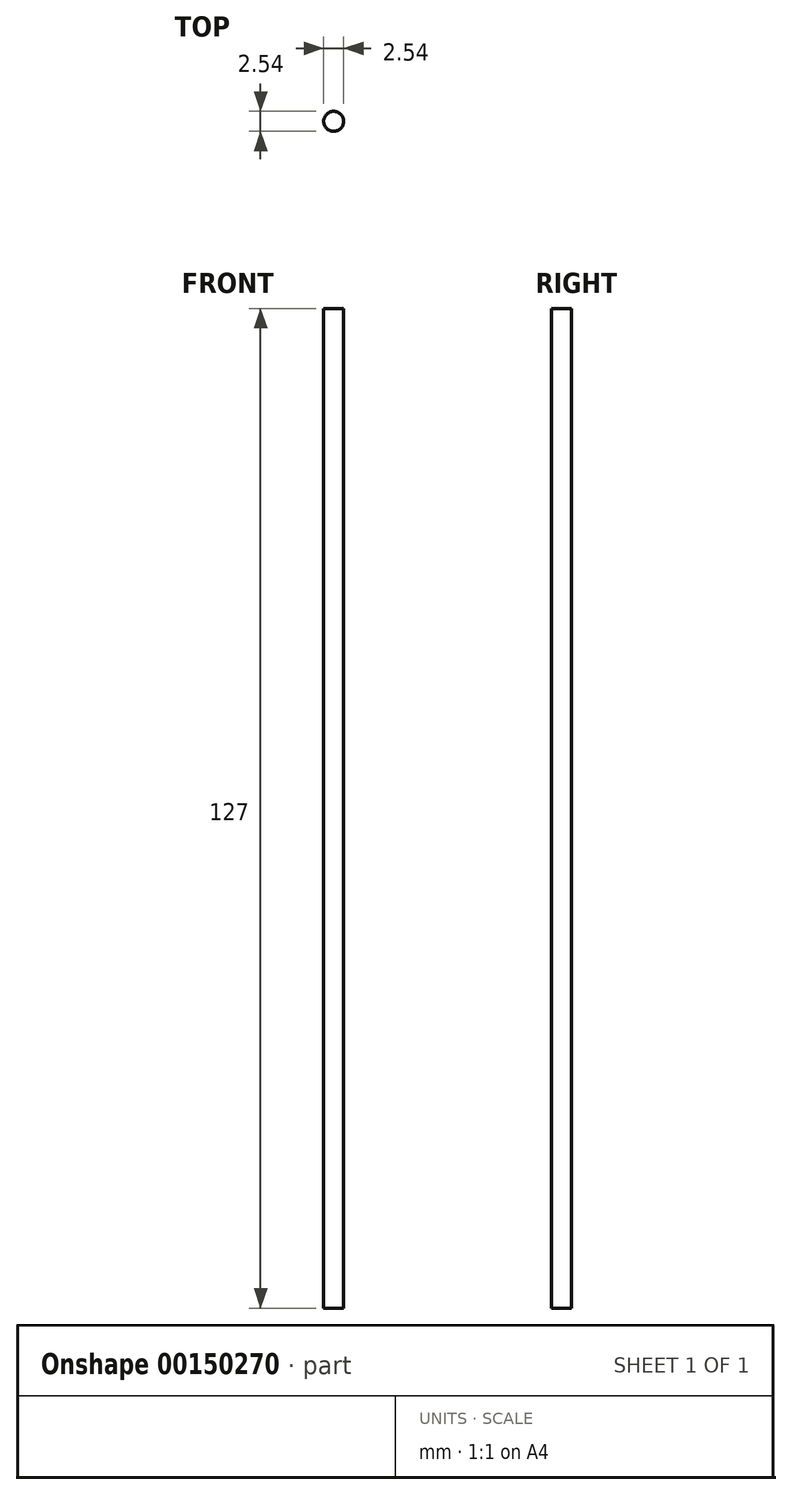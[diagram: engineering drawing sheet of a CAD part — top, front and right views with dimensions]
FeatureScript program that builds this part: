
annotation { "Feature Type Name" : "Feature", "Feature Type Description" : "" }
export const myFeature = defineFeature(function(context is Context, id is Id, definition is map)
    precondition{}
    {
        {
            var Q0;
            Q0=qCreatedBy(makeId("Top.planeOp"),FACE);
            var sketch = newSketch(context, id + "F0", { "sketchPlane" : qUnion([Q0])});
            skCircle(sketch, "E0", {"center": v(0, 0) * mm, "radius": 1.27 * mm});
            skSolve(sketch);
        }
        {
            var Q0;
            Q0=sQuery(id+"F0.wireOp",EDGE,"E0");
            extrude(context, id + "F1", {"bodyType" : ToolBodyType.SURFACE, "surfaceEntities" : qUnion([Q0]), "depth" : 127 * mm});
        }
    });
